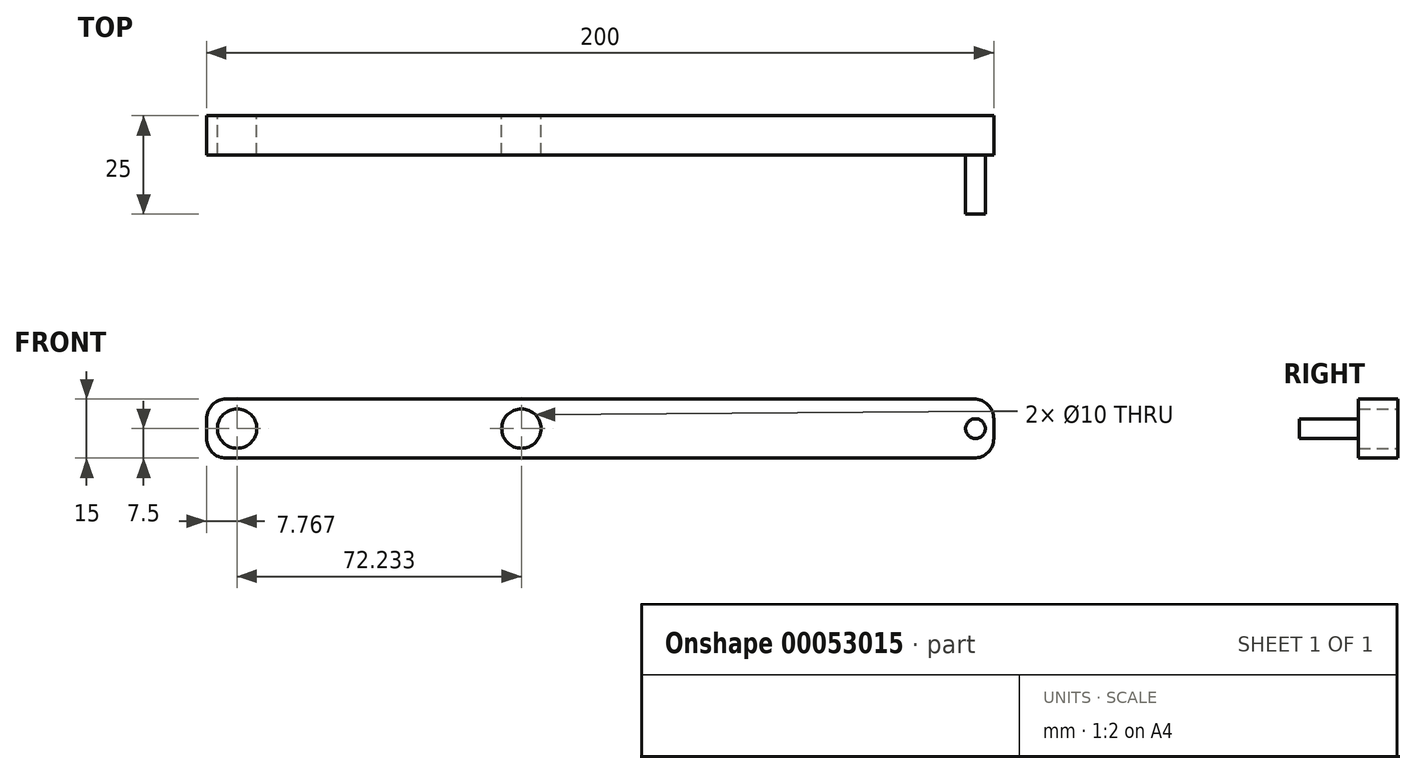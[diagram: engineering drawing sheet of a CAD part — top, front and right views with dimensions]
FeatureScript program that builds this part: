
annotation { "Feature Type Name" : "Feature", "Feature Type Description" : "" }
export const myFeature = defineFeature(function(context is Context, id is Id, definition is map)
    precondition{}
    {
        {
            var Q0;
            Q0=qCreatedBy(makeId("Front.planeOp"),FACE);
            var sketch = newSketch(context, id + "F0", { "sketchPlane" : qUnion([Q0])});
            skLineSegment(sketch, "E0.bottom", {"start": v(5, 0) * mm, "end": v(195, 0) * mm});
            skLineSegment(sketch, "E0.top", {"start": v(5, 15) * mm, "end": v(195, 15) * mm});
            skLineSegment(sketch, "E0.left", {"start": v(0, 5) * mm, "end": v(0, 10) * mm});
            skLineSegment(sketch, "E0.right", {"start": v(200, 5) * mm, "end": v(200, 10) * mm});
            skPoint(sketch, "E1.visualSharp", {"position": v(0, 15) * mm});
            skArc(sketch, "E1.filletArc", {"start": v(5, 15) * mm, "mid": v(1.46, 13.54) * mm, "end": v(0, 10) * mm});
            skPoint(sketch, "E2.visualSharp", {"position": v(0, 0) * mm});
            skArc(sketch, "E2.filletArc", {"start": v(0, 5) * mm, "mid": v(1.46, 1.46) * mm, "end": v(5, 0) * mm});
            skPoint(sketch, "E3.visualSharp", {"position": v(200, 0) * mm});
            skArc(sketch, "E3.filletArc", {"start": v(195, 0) * mm, "mid": v(198.54, 1.46) * mm, "end": v(200, 5) * mm});
            skPoint(sketch, "E4.visualSharp", {"position": v(200, 15) * mm});
            skArc(sketch, "E4.filletArc", {"start": v(200, 10) * mm, "mid": v(198.54, 13.54) * mm, "end": v(195, 15) * mm});
            skCircle(sketch, "E5", {"center": v(7.77, 7.5) * mm, "radius": 5 * mm});
            skPoint(sketch, "E5.centerSnap0", {"position": v(0, 7.5) * mm});
            skCircle(sketch, "E6", {"center": v(80, 7.5) * mm, "radius": 5 * mm});
            skSolve(sketch);
        }
        {
            var Q0;
            Q0=makeQuery(id+"F0.imprint","IMPRINT",FACE,{"disambiguationData":[TD([[makeQuery(id+"F0.imprint","IMPRINT",EDGE,{"derivedFrom":sQuery(id+"F0.wireOp",EDGE,"E0.bottom")}),1.0]])]});
            extrude(context, id + "F1", {"entities" : qUnion([Q0]), "depth" : 10 * mm});
        }
        {
            var Q0;
            Q0=makeQuery(id+"F1.opExtrude","CAP_FACE",FACE,{"disambiguationData":[OSD([sQuery(id+"F0.wireOp",EDGE,"E0.bottom"),sQuery(id+"F0.wireOp",EDGE,"E0.top"),sQuery(id+"F0.wireOp",EDGE,"E0.left"),sQuery(id+"F0.wireOp",EDGE,"E0.right"),sQuery(id+"F0.wireOp",EDGE,"E1.filletArc"),sQuery(id+"F0.wireOp",EDGE,"E2.filletArc"),sQuery(id+"F0.wireOp",EDGE,"E3.filletArc"),sQuery(id+"F0.wireOp",EDGE,"E4.filletArc"),sQuery(id+"F0.wireOp",EDGE,"E5")])],"isStart":false});
            var sketch = newSketch(context, id + "F2", { "sketchPlane" : qUnion([Q0])});
            skCircle(sketch, "E7", {"center": v(195.35, 7.5) * mm, "radius": 2.5 * mm});
            skPoint(sketch, "E7.centerSnap0", {"position": v(200, 7.5) * mm});
            skSolve(sketch);
        }
        {
            var Q0;
            Q0=makeQuery(id+"F2.imprint","IMPRINT",FACE,{"disambiguationData":[TD([[makeQuery(id+"F2.imprint","IMPRINT",EDGE,{"derivedFrom":sQuery(id+"F2.wireOp",EDGE,"E7")}),1.0]])]});
            extrude(context, id + "F3", {"entities" : qUnion([Q0]), "operationType" : NewBodyOperationType.ADD, "depth" : 15 * mm});
        }
    });
